# Revit family: NX_OMNI_Indoor_Sensor_Module
name_source: partatom
category: Communication Devices
units: mm (PartAtom-declared; Revit-internal decimal feet)

## family parameters
Cut with Voids When Loaded = No
Host = Face
Maintain Annotation Orientation = No
OmniClass Number = 23.85.80.11.27
OmniClass Title = Lighting Controls
Part Type = Normal
Room Calculation Point = No
Round Connector Dimension = Use Diameter
Shared = Yes

## types (1)
- NX_OMNI_Indoor_Sensor_Module
    Assembly Code = D5090
    Certifications = Bluetooth Version 4.1,FCC Part 15.247,FCC ID: YH9NXSMP,
IC: 9044A-NXSMP
    Default Elevation = 48 "
    Description = The Control Solutions NXSMP-OMNI Module provides a unique solution for integrating automatic control functions directly into a luminaire.
    Housing Material = Paint -  Matte White
    Manufacturer = NX Lighting Controls
    Model = NX OMNI Indoor/Outdoor Sensor Module
    Mounting = Mounts in 1.5” diameter aperture, secured by supplied nut on threaded body Recommended max mounting height: 16’ [4.87 m], min 8’ [2.43 m]
    Power Requirements = 12VDC, 30 mA supplied by NXFM or NXRC
    Sensing Element = Paint - Gray Smooth
    Technology = Passive Infrared
    Timer Timeout = Automatic mode:1 sec - 20 min
    Type Comments = Sensor Module
    URL = https://www.currentlighting.com
    Warranty = 5-Years Warranty

## geometry (parser evidence)
native form markers: Sweep x2
no freeform markers — native parametric forms only
